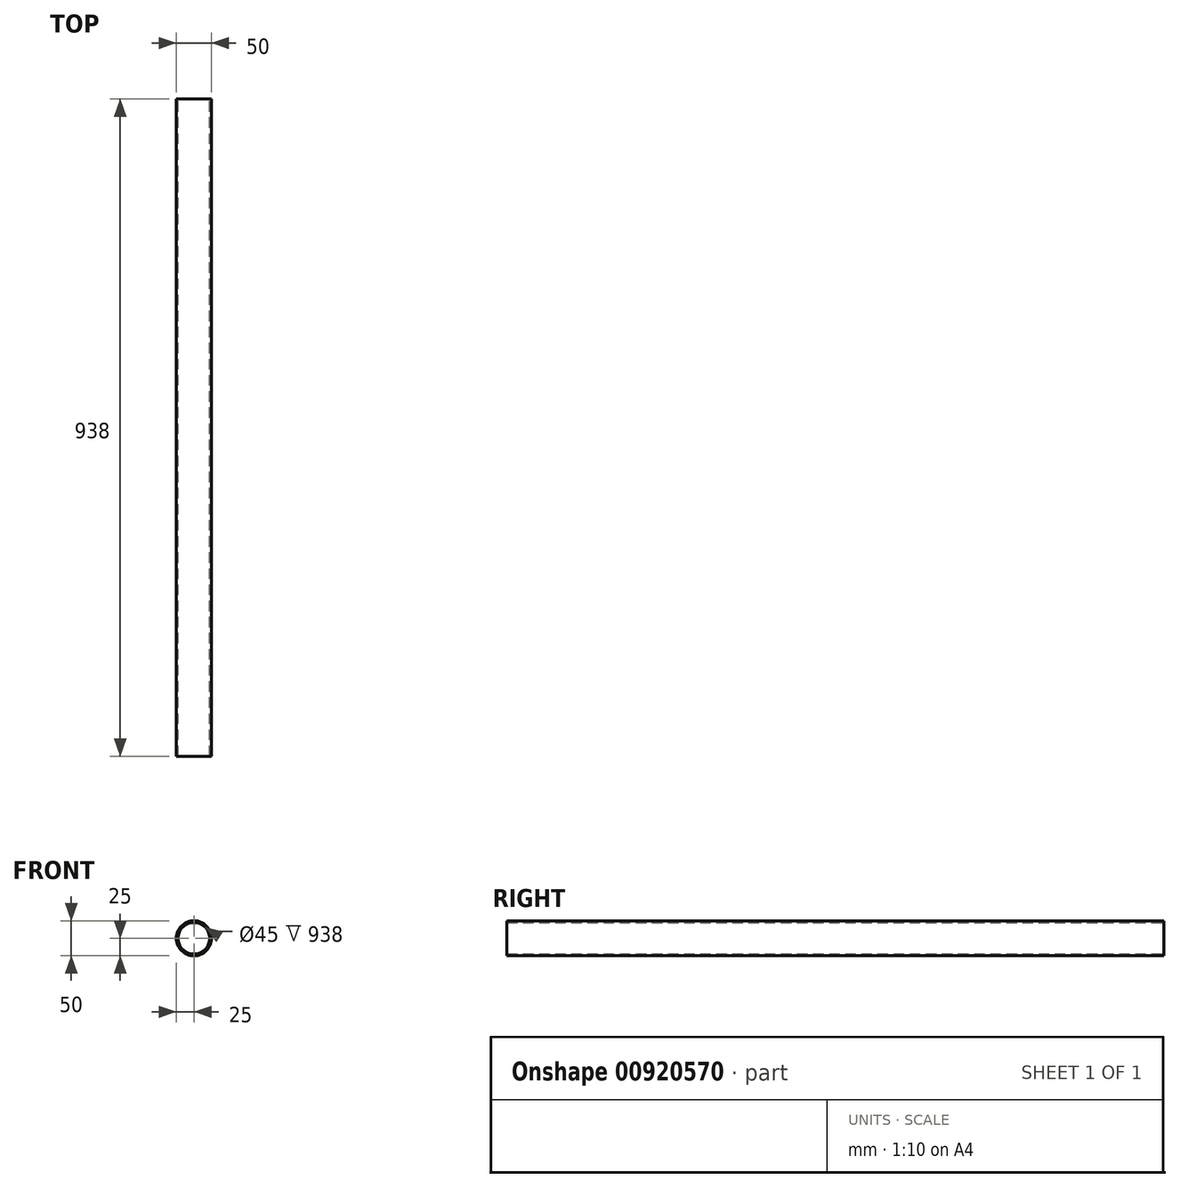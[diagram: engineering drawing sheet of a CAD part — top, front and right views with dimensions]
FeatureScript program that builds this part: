
annotation { "Feature Type Name" : "Feature", "Feature Type Description" : "" }
export const myFeature = defineFeature(function(context is Context, id is Id, definition is map)
    precondition{}
    {
        {
            var Q0;
            Q0=qCreatedBy(makeId("Front.planeOp"),FACE);
            var sketch = newSketch(context, id + "F0", { "sketchPlane" : qUnion([Q0])});
            skCircle(sketch, "E0", {"center": v(0, 0) * mm, "radius": 25 * mm});
            skCircle(sketch, "E1", {"center": v(0, 0) * mm, "radius": 22.5 * mm});
            skSolve(sketch);
        }
        {
            var Q0;
            Q0=makeQuery(id+"F0.imprint","IMPRINT",FACE,{"disambiguationData":[TD([[makeQuery(id+"F0.imprint","IMPRINT",EDGE,{"derivedFrom":sQuery(id+"F0.wireOp",EDGE,"E0")}),1.0]])]});
            extrude(context, id + "F1", {"entities" : qUnion([Q0]), "depth" : 938 * mm, "offsetDistance" : 25 * mm, "symmetric" : true});
        }
    });
